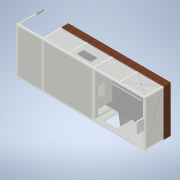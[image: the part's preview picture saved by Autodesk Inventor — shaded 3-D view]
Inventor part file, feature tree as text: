
AUTODESK INVENTOR PART (.ipt)
format: ipt  version: 2021 (Build 250183000, 183)  size: 729,088 bytes
history: mixed  units: in
note: dims shown in document units (in); Inventor stores cm internally (conversion verified against a paired STEP export)
features: extrude x3, sketch x3, other x1, imported_body x1
ambient origin geometry x8: Origin, YZ Plane, XZ Plane, XY Plane, X Axis, Y Axis, Z Axis, Center Point
bodies: Solid1 (imported_parasolid)
feature tree (8):
  other  "Building"
  extrude  "Extrusion1"  Depth=0.1969in TaperAngle=0.0deg
  extrude  "Extrusion2"  Depth=0.0197in
  extrude  "Extrusion3"  [1 undecoded]
  sketch  "Sketch1"  dims[d0=0.1969in d1=0.0in d2=0.1969in d3=0.0in]
  sketch  "Sketch2"  dims[d4=0.9843in d5=0.0in d6=0.0197in]
  sketch  "Sketch3"  dims[d7=1.9685in]
  imported_body  NMx_Import_Brep_tag  [imported B-rep: ~198 faces, bbox_mm=[18000.5, 8500.5, 4700.0]]
note: 1 required parameter value undecoded (feature->parameter linkage not recoverable at this tier; creation-order binding heuristic only, values carry confidence <= 0.55)
